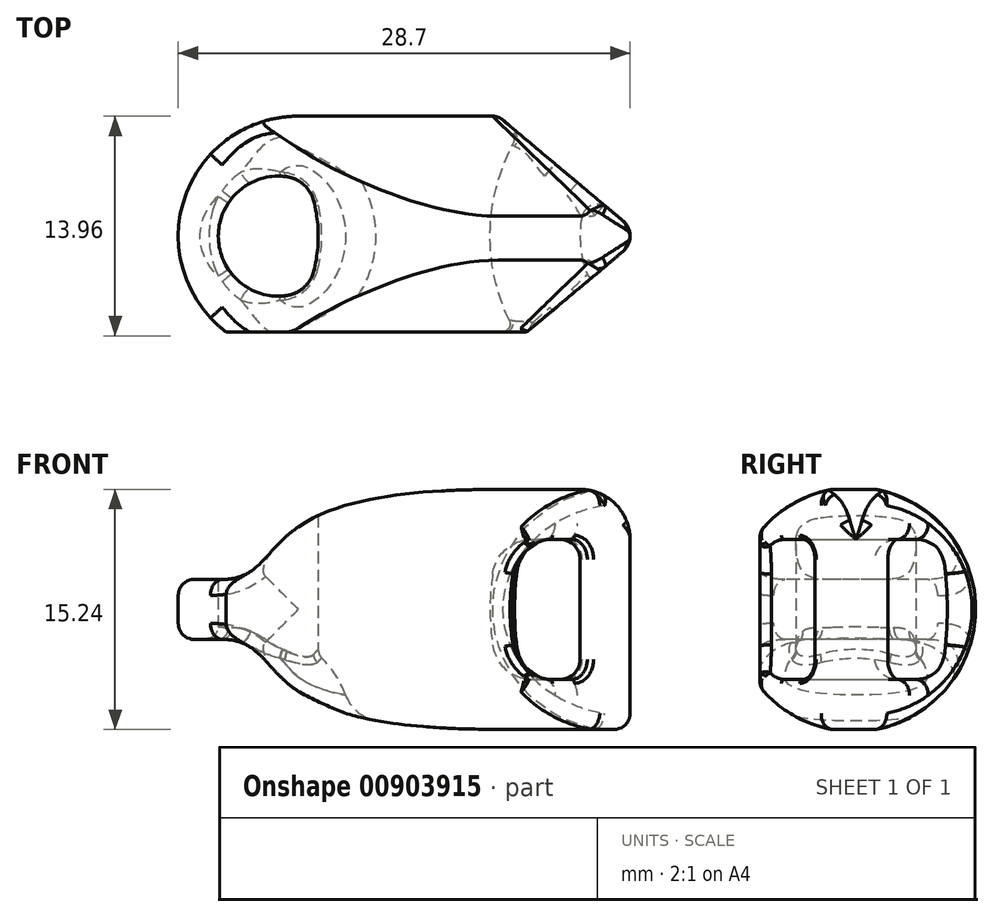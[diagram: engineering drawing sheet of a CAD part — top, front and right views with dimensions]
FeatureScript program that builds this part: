
annotation { "Feature Type Name" : "Feature", "Feature Type Description" : "" }
export const myFeature = defineFeature(function(context is Context, id is Id, definition is map)
    precondition{}
    {
        {
            var Q0;
            Q0=qCreatedBy(makeId("Top.planeOp"),FACE);
            var sketch = newSketch(context, id + "F0", { "sketchPlane" : qUnion([Q0])});
            skLineSegment(sketch, "E0", {"start": v(-6.35, 15.24) * mm, "end": v(6.35, 15.24) * mm});
            skLineSegment(sketch, "E1", {"start": v(-6.35, 0) * mm, "end": v(6.35, 0) * mm});
            skLineSegment(sketch, "E2", {"start": v(6.35, 0) * mm, "end": v(15.43, 7.62) * mm});
            skLineSegment(sketch, "E3", {"start": v(15.43, 7.62) * mm, "end": v(6.35, 15.24) * mm});
            skArc(sketch, "E4", {"start": v(-6.35, 15.24) * mm, "mid": v(-13.97, 7.62) * mm, "end": v(-6.35, 0) * mm});
            skSolve(sketch);
        }
        {
            var Q0;
            Q0 = qSketchRegion(id + "F0", true);
            extrude(context, id + "F1", {"entities" : qUnion([Q0]), "depth" : 15.24 * mm, "offsetDistance" : 25.4 * mm});
        }
        {
            var Q0;
            Q0=makeQuery(id+"F1.opExtrude","SWEPT_EDGE",EDGE,{"disambiguationData":[OSD([sQuery(id+"F0.wireOp",EDGE,"E2"),sQuery(id+"F0.wireOp",EDGE,"E3")])]});
            fillet(context, id + "F2", {"entities" : qUnion([Q0]), "radius" : 1.27 * mm, "tangentPropagation" : true, "allowEdgeOverflow" : false});
        }
        {
            var Q0;
            Q0=qCreatedBy(makeId("Front.planeOp"),FACE);
            cPlane(context, id + "F3", {"entities" : qUnion([Q0]), "cplaneType" : CPlaneType.OFFSET, "offset" : 7.62 * mm, "oppositeDirection" : true, "width" : 152.4 * mm, "height" : 152.4 * mm});
        }
        {
            var Q0;
            Q0=qCreatedBy(id+"F3.planeOp",FACE);
            var sketch = newSketch(context, id + "F4", { "sketchPlane" : qUnion([Q0])});
            skArc(sketch, "E5", {"start": v(6, 9.89) * mm, "mid": v(5.84, 7.62) * mm, "end": v(6, 5.35) * mm});
            skLineSegment(sketch, "E6", {"start": v(11.55, 4.45) * mm, "end": v(11.55, 10.8) * mm});
            skLineSegment(sketch, "E7.0.0", {"start": v(14.27, 15.24) * mm, "end": v(14.73, 15.24) * mm, "construction": true});
            skLineSegment(sketch, "E7.0.1", {"start": v(14.27, 0) * mm, "end": v(14.27, 15.24) * mm, "construction": true});
            skLineSegment(sketch, "E7.0.2", {"start": v(14.27, 0) * mm, "end": v(14.73, 0) * mm, "construction": true});
            skLineSegment(sketch, "E7.0.3", {"start": v(14.27, 0) * mm, "end": v(14.27, 15.24) * mm, "construction": true});
            skLineSegment(sketch, "E8", {"start": v(10.28, 12.06) * mm, "end": v(8.51, 12.06) * mm});
            skLineSegment(sketch, "E9", {"start": v(10.28, 3.17) * mm, "end": v(8.51, 3.17) * mm});
            skPoint(sketch, "E10.visualSharp", {"position": v(6.47, 12.06) * mm});
            skArc(sketch, "E10.filletArc", {"start": v(8.51, 12.06) * mm, "mid": v(6.85, 11.45) * mm, "end": v(6, 9.89) * mm});
            skPoint(sketch, "E11.visualSharp", {"position": v(6.47, 3.17) * mm});
            skArc(sketch, "E11.filletArc", {"start": v(6, 5.35) * mm, "mid": v(6.85, 3.8) * mm, "end": v(8.51, 3.17) * mm});
            skPoint(sketch, "E12.visualSharp", {"position": v(11.55, 3.18) * mm});
            skArc(sketch, "E12.filletArc", {"start": v(10.28, 3.17) * mm, "mid": v(11.18, 3.55) * mm, "end": v(11.55, 4.45) * mm});
            skPoint(sketch, "E13.visualSharp", {"position": v(11.55, 12.06) * mm});
            skArc(sketch, "E13.filletArc", {"start": v(11.55, 10.8) * mm, "mid": v(11.18, 11.7) * mm, "end": v(10.28, 12.06) * mm});
            skLineSegment(sketch, "E14", {"start": v(18.27, 11.8) * mm, "end": v(18.27, -2.1) * mm, "construction": true});
            skSolve(sketch);
        }
        {
            var Q0;
            Q0 = qSketchRegion(id + "F4", true);
            var Q1;
            Q1=sQuery(id+"F4.wireOp",EDGE,"E14");
            revolve(context, id + "F5", {"operationType" : NewBodyOperationType.REMOVE, "surfaceOperationType" : NewSurfaceOperationType.NEW, "entities" : qUnion([Q0]), "axis" : qUnion([Q1]), "revolveType" : RevolveType.FULL, "oppositeDirection" : true});
        }
        {
            var Q0;
            Q0=makeQuery(id+"F1.opExtrude","SWEPT_FACE",FACE,{"disambiguationData":[OSD([sQuery(id+"F0.wireOp",EDGE,"E1")])]});
            var sketch = newSketch(context, id + "F6", { "sketchPlane" : qUnion([Q0])});
            skLineSegment(sketch, "E15", {"start": v(-15.35, 7.62) * mm, "end": v(17.07, 7.62) * mm, "construction": true});
            skLineSegment(sketch, "E16.0", {"start": v(-15.35, 5.71) * mm, "end": v(17.07, 5.71) * mm, "construction": true});
            skLineSegment(sketch, "E17.0", {"start": v(-15.35, 9.53) * mm, "end": v(17.07, 9.53) * mm, "construction": true});
            skLineSegment(sketch, "E18.0", {"start": v(11.8, 11.94) * mm, "end": v(11.8, 11.94) * mm});
            skPoint(sketch, "E19.first.point", {"position": v(-13.97, 9.53) * mm});
            skLineSegment(sketch, "E20.0", {"start": v(-6.35, 15.24) * mm, "end": v(6.35, 15.24) * mm, "construction": true});
            skLineSegment(sketch, "E21.0", {"start": v(-6.35, 0) * mm, "end": v(-13.97, 0) * mm, "construction": true});
            skLineSegment(sketch, "E22", {"start": v(-13.97, 0) * mm, "end": v(-13.97, 14.89) * mm, "construction": true});
            skLineSegment(sketch, "E23.0", {"start": v(-6.35, 0) * mm, "end": v(2.29, 0) * mm, "construction": true});
            skLineSegment(sketch, "E24", {"start": v(-11.18, 9.53) * mm, "end": v(-16.26, 9.53) * mm});
            skLineSegment(sketch, "E25", {"start": v(-16.26, 9.53) * mm, "end": v(-15.86, 16.25) * mm});
            skLineSegment(sketch, "E26.MirrorCS", {"start": v(-15.35, 5.72) * mm, "end": v(17.07, 5.72) * mm, "construction": true});
            skLineSegment(sketch, "E27.MirrorCS", {"start": v(-16.26, 5.72) * mm, "end": v(-15.86, -1) * mm});
            skLineSegment(sketch, "E28.MirrorCS", {"start": v(-11.18, 5.71) * mm, "end": v(-16.26, 5.71) * mm});
            skFitSpline(sketch, "E29", {"points": [v(6.35, 15.24) * mm, v(-8.08, 11.26) * mm, v(-11.18, 9.53) * mm], "startDerivative": vector(-47.28, 0) * mm, "endDerivative": vector(-14.56, 0) * mm});
            skLineSegment(sketch, "E30", {"start": v(-15.86, 16.25) * mm, "end": v(6.35, 15.24) * mm});
            skLineSegment(sketch, "E31.MirrorCS", {"start": v(-15.86, -1) * mm, "end": v(6.35, 0) * mm});
            skFitSpline(sketch, "E32.MirrorCS", {"points": [v(6.35, 0) * mm, v(-8.08, 3.98) * mm, v(-11.18, 5.71) * mm], "startDerivative": vector(-47.28, 0) * mm, "endDerivative": vector(-14.56, 0) * mm});
            skSolve(sketch);
        }
        {
            var Q0;
            Q0 = qSketchRegion(id + "F6", true);
            extrude(context, id + "F7", {"entities" : qUnion([Q0]), "operationType" : NewBodyOperationType.REMOVE, "oppositeDirection" : true, "depth" : 25.4 * mm, "offsetDistance" : 25.4 * mm});
        }
        {
            var Q0;
            Q0=qCreatedBy(makeId("Right.planeOp"),FACE);
            var sketch = newSketch(context, id + "F8", { "sketchPlane" : qUnion([Q0])});
            skCircle(sketch, "E33", {"center": v(7.5, 7.62) * mm, "radius": 16.21 * mm});
            skLineSegment(sketch, "E34.0", {"start": v(15.24, 12.86) * mm, "end": v(15.24, 12.86) * mm});
            skLineSegment(sketch, "E34.1", {"start": v(15.24, 15.24) * mm, "end": v(0, 15.24) * mm, "construction": true});
            skLineSegment(sketch, "E34.2", {"start": v(0, 12.86) * mm, "end": v(0, 2.38) * mm, "construction": true});
            skLineSegment(sketch, "E34.3", {"start": v(15.24, 0) * mm, "end": v(0, 0) * mm, "construction": true});
            skArc(sketch, "E35", {"start": v(1.52, 2.68) * mm, "mid": v(15.24, 7.62) * mm, "end": v(1.52, 12.56) * mm});
            skLineSegment(sketch, "E36", {"start": v(1.52, 12.56) * mm, "end": v(1.52, 2.68) * mm});
            skSolve(sketch);
        }
        {
            var Q0;
            Q0 = qSketchRegion(id + "F8", true);
            extrude(context, id + "F9", {"entities" : qUnion([Q0]), "operationType" : NewBodyOperationType.REMOVE, "endBound" : BoundingType.SYMMETRIC, "oppositeDirection" : true, "depth" : 127 * mm, "offsetDistance" : 25.4 * mm});
        }
        {
            var Q0;
            Q0=makeQuery(id+"F7.boolean.opBoolean","COPY",FACE,{"derivedFrom":makeQuery(id+"F7.opExtrude","SWEPT_FACE",FACE,{"disambiguationData":[OSD([sQuery(id+"F6.wireOp",EDGE,"E28.MirrorCS")])]})});
            var sketch = newSketch(context, id + "F10", { "sketchPlane" : qUnion([Q0])});
            skLineSegment(sketch, "E37.0", {"start": v(-11.18, -1.72) * mm, "end": v(-11.18, -1.72) * mm});
            skArc(sketch, "E38", {"start": v(-5.37, -9.87) * mm, "mid": v(-5.08, -7.62) * mm, "end": v(-5.37, -5.37) * mm});
            skLineSegment(sketch, "E39", {"start": v(-7.37, -0.39) * mm, "end": v(-7.37, -15.77) * mm, "construction": true});
            skArc(sketch, "E40", {"start": v(-7.07, -3.85) * mm, "mid": v(-11.43, -7.62) * mm, "end": v(-7.07, -11.39) * mm});
            skArc(sketch, "E41", {"start": v(-5.37, -5.37) * mm, "mid": v(-5.99, -4.36) * mm, "end": v(-7.07, -3.85) * mm});
            skArc(sketch, "E42", {"start": v(-7.07, -11.39) * mm, "mid": v(-5.99, -10.88) * mm, "end": v(-5.37, -9.87) * mm});
            skSolve(sketch);
        }
        {
            var Q0;
            Q0 = qSketchRegion(id + "F10", true);
            extrude(context, id + "F11", {"entities" : qUnion([Q0]), "operationType" : NewBodyOperationType.REMOVE, "endBound" : BoundingType.SYMMETRIC, "oppositeDirection" : true, "depth" : 25.4 * mm, "offsetDistance" : 25.4 * mm});
        }
        {
            var Q0;
            Q0=qCreatedBy(makeId("Front.planeOp"),FACE);
            cPlane(context, id + "F12", {"entities" : qUnion([Q0]), "cplaneType" : CPlaneType.OFFSET, "offset" : 2.54 * mm, "oppositeDirection" : true, "width" : 152.4 * mm, "height" : 152.4 * mm});
        }
        {
            var Q0;
            Q0=qCreatedBy(id+"F12.planeOp",FACE);
            var sketch = newSketch(context, id + "F13", { "sketchPlane" : qUnion([Q0])});
            skCircle(sketch, "E43", {"center": v(0, 4.3) * mm, "radius": 43.05 * mm});
            skSolve(sketch);
        }
        {
            var Q0;
            Q0=qCreatedBy(makeId("Top.planeOp"),FACE);
            var sketch = newSketch(context, id + "F14", { "sketchPlane" : qUnion([Q0])});
            skArc(sketch, "E44", {"start": v(-9.3, 1.27) * mm, "mid": v(-2.96, 7.62) * mm, "end": v(-9.3, 13.97) * mm});
            skLineSegment(sketch, "E45", {"start": v(-9.3, 17.15) * mm, "end": v(-9.3, 13.97) * mm, "construction": true});
            skLineSegment(sketch, "E46", {"start": v(-9.3, 13.97) * mm, "end": v(-9.3, 1.27) * mm});
            skSolve(sketch);
        }
        {
            var Q0;
            Q0=makeQuery(id+"F14.imprint","IMPRINT",FACE,{"disambiguationData":[TD([[makeQuery(id+"F14.imprint","IMPRINT",EDGE,{"derivedFrom":sQuery(id+"F14.wireOp",EDGE,"E44")}),1.0]])]});
            var Q1;
            Q1=sQuery(id+"F14.wireOp",EDGE,"E45");
            revolve(context, id + "F15", {"operationType" : NewBodyOperationType.REMOVE, "surfaceOperationType" : NewSurfaceOperationType.NEW, "entities" : qUnion([Q0]), "axis" : qUnion([Q1]), "revolveType" : RevolveType.FULL, "oppositeDirection" : true});
        }
        {
            var Q0;
            Q0=qCreatedBy(makeId("Top.planeOp"),FACE);
            cPlane(context, id + "F16", {"entities" : qUnion([Q0]), "cplaneType" : CPlaneType.OFFSET, "offset" : 7.62 * mm, "width" : 152.4 * mm, "height" : 152.4 * mm});
        }
        {
            var Q0;
            Q0=makeQuery(id+"FS2piOo9BQHkGEu_1.1.F15.boolean.opBoolean","INTERSECT",EDGE,{"disambiguationData":[OD(1.0)],"derivedFrom":[makeQuery(id+"F7.boolean.opBoolean","COPY",FACE,{"derivedFrom":makeQuery(id+"F7.opExtrude","SWEPT_FACE",FACE,{"disambiguationData":[OSD([sQuery(id+"F6.wireOp",EDGE,"E29")])]})}),makeQuery(id+"FS2piOo9BQHkGEu_1.1.F15.opRevolve","SWEPT_FACE",FACE,{"disambiguationData":[OSD([sQuery(id+"F14.wireOp",EDGE,"E44")])]})]});
            var Q1;
            Q1=makeQuery(id+"F15.boolean.opBoolean","INTERSECT",EDGE,{"disambiguationData":[OD(1.0)],"derivedFrom":[makeQuery(id+"F7.boolean.opBoolean","COPY",FACE,{"derivedFrom":makeQuery(id+"F7.opExtrude","SWEPT_FACE",FACE,{"disambiguationData":[OSD([sQuery(id+"F6.wireOp",EDGE,"E32.MirrorCS")])]})}),makeQuery(id+"F15.opRevolve","SWEPT_FACE",FACE,{"disambiguationData":[OSD([sQuery(id+"F14.wireOp",EDGE,"E44")])]})]});
            fillet(context, id + "F17", {"entities" : qUnion([Q0, Q1]), "radius" : 2.54 * mm, "allowEdgeOverflow" : false});
        }
        {
            var Q0;
            Q0=makeQuery(id+"F7.boolean.opBoolean","INTERSECT",EDGE,{"derivedFrom":[makeQuery(id+"F1.opExtrude","SWEPT_FACE",FACE,{"disambiguationData":[OSD([sQuery(id+"F0.wireOp",EDGE,"E4")])]}),makeQuery(id+"F7.opExtrude","SWEPT_FACE",FACE,{"disambiguationData":[OSD([sQuery(id+"F6.wireOp",EDGE,"E24")])]})]});
            var Q1;
            Q1=makeQuery(id+"F7.boolean.opBoolean","INTERSECT",EDGE,{"derivedFrom":[makeQuery(id+"F1.opExtrude","SWEPT_FACE",FACE,{"disambiguationData":[OSD([sQuery(id+"F0.wireOp",EDGE,"E4")])]}),makeQuery(id+"F7.opExtrude","SWEPT_FACE",FACE,{"disambiguationData":[OSD([sQuery(id+"F6.wireOp",EDGE,"E28.MirrorCS")])]})]});
            var Q2;
            Q2=makeQuery(id+"F9.boolean.opBoolean","INTERSECT",EDGE,{"disambiguationData":[OD(1.0)],"derivedFrom":[makeQuery(id+"F1.opExtrude","SWEPT_FACE",FACE,{"disambiguationData":[OSD([sQuery(id+"F0.wireOp",EDGE,"E3")])]}),makeQuery(id+"F9.opExtrude","SWEPT_FACE",FACE,{"disambiguationData":[OSD([sQuery(id+"F8.wireOp",EDGE,"E35")])]})]});
            var Q3;
            {var subQ0=sQuery(id+"F0.wireOp",EDGE,"E3");var subQ1=sQuery(id+"F0.wireOp",EDGE,"E2");Q3=makeQuery(id+"F2.opFillet","BLEND_EDGE",EDGE,{"blendedFrom":[makeQuery(id+"F1.opExtrude","SWEPT_EDGE",EDGE,{"disambiguationData":[OSD([subQ1,subQ0])]}),makeQuery(id+"F1.opExtrude","CAP_FACE",FACE,{"disambiguationData":[OSD([sQuery(id+"F0.wireOp",EDGE,"E0"),sQuery(id+"F0.wireOp",EDGE,"E1"),subQ1,subQ0,sQuery(id+"F0.wireOp",EDGE,"E4")])],"isStart":false})],"blendedInto":[makeQuery(id+"F1.opExtrude","CAP_FACE",FACE,{"disambiguationData":[OSD([sQuery(id+"F0.wireOp",EDGE,"E0"),sQuery(id+"F0.wireOp",EDGE,"E1"),subQ1,subQ0,sQuery(id+"F0.wireOp",EDGE,"E4")])],"isStart":false})]});}
            var Q4;
            Q4=makeQuery(id+"F9.boolean.opBoolean","INTERSECT",EDGE,{"disambiguationData":[OD(0.0)],"derivedFrom":[makeQuery(id+"F1.opExtrude","SWEPT_FACE",FACE,{"disambiguationData":[OSD([sQuery(id+"F0.wireOp",EDGE,"E3")])]}),makeQuery(id+"F9.opExtrude","SWEPT_FACE",FACE,{"disambiguationData":[OSD([sQuery(id+"F8.wireOp",EDGE,"E35")])]})]});
            var Q5;
            {var subQ0=sQuery(id+"F0.wireOp",EDGE,"E3");var subQ1=sQuery(id+"F0.wireOp",EDGE,"E2");Q5=makeQuery(id+"F2.opFillet","BLEND_EDGE",EDGE,{"blendedFrom":[makeQuery(id+"F1.opExtrude","SWEPT_EDGE",EDGE,{"disambiguationData":[OSD([subQ1,subQ0])]}),makeQuery(id+"F1.opExtrude","CAP_FACE",FACE,{"disambiguationData":[OSD([sQuery(id+"F0.wireOp",EDGE,"E0"),sQuery(id+"F0.wireOp",EDGE,"E1"),subQ1,subQ0,sQuery(id+"F0.wireOp",EDGE,"E4")])],"isStart":true})],"blendedInto":[makeQuery(id+"F1.opExtrude","CAP_FACE",FACE,{"disambiguationData":[OSD([sQuery(id+"F0.wireOp",EDGE,"E0"),sQuery(id+"F0.wireOp",EDGE,"E1"),subQ1,subQ0,sQuery(id+"F0.wireOp",EDGE,"E4")])],"isStart":true})]});}
            var Q6;
            Q6=makeQuery(id+"F9.boolean.opBoolean","INTERSECT",EDGE,{"disambiguationData":[OD(0.0)],"derivedFrom":[makeQuery(id+"F1.opExtrude","SWEPT_FACE",FACE,{"disambiguationData":[OSD([sQuery(id+"F0.wireOp",EDGE,"E2")])]}),makeQuery(id+"F9.opExtrude","SWEPT_FACE",FACE,{"disambiguationData":[OSD([sQuery(id+"F8.wireOp",EDGE,"E35")])]})]});
            var Q7;
            Q7=makeQuery(id+"F9.boolean.opBoolean","INTERSECT",EDGE,{"disambiguationData":[OD(1.0)],"derivedFrom":[makeQuery(id+"F1.opExtrude","SWEPT_FACE",FACE,{"disambiguationData":[OSD([sQuery(id+"F0.wireOp",EDGE,"E2")])]}),makeQuery(id+"F9.opExtrude","SWEPT_FACE",FACE,{"disambiguationData":[OSD([sQuery(id+"F8.wireOp",EDGE,"E35")])]})]});
            var Q8;
            {var subQ0=sQuery(id+"F8.wireOp",EDGE,"E36");var subQ1=sQuery(id+"F8.wireOp",EDGE,"E35");Q8=makeQuery(id+"F9.boolean.opBoolean","COPY",EDGE,{"derivedFrom":makeQuery(id+"F9.opExtrude","SWEPT_EDGE",EDGE,{"disambiguationData":[OSD([subQ1,subQ0]),TDD([makeQuery(id+"F8.imprint","INTERSECT",VERTEX,{"disambiguationData":[OD(1.0)],"derivedFrom":[subQ1,subQ0]})])]})});}
            var Q9;
            {var subQ0=sQuery(id+"F8.wireOp",EDGE,"E36");var subQ1=sQuery(id+"F8.wireOp",EDGE,"E35");Q9=makeQuery(id+"F9.boolean.opBoolean","COPY",EDGE,{"derivedFrom":makeQuery(id+"F9.opExtrude","SWEPT_EDGE",EDGE,{"disambiguationData":[OSD([subQ1,subQ0]),TDD([makeQuery(id+"F8.imprint","INTERSECT",VERTEX,{"disambiguationData":[OD(0.0)],"derivedFrom":[subQ1,subQ0]})])]})});}
            var Q10;
            Q10=makeQuery(id+"F9.boolean.opBoolean","INTERSECT",EDGE,{"disambiguationData":[OD(0.0)],"derivedFrom":[makeQuery(id+"F1.opExtrude","SWEPT_FACE",FACE,{"disambiguationData":[OSD([sQuery(id+"F0.wireOp",EDGE,"E0")])]}),makeQuery(id+"F9.opExtrude","SWEPT_FACE",FACE,{"disambiguationData":[OSD([sQuery(id+"F8.wireOp",EDGE,"E35")])]})]});
            var Q11;
            Q11=makeQuery(id+"F9.boolean.opBoolean","INTERSECT",EDGE,{"disambiguationData":[OD(1.0)],"derivedFrom":[makeQuery(id+"F1.opExtrude","SWEPT_FACE",FACE,{"disambiguationData":[OSD([sQuery(id+"F0.wireOp",EDGE,"E0")])]}),makeQuery(id+"F9.opExtrude","SWEPT_FACE",FACE,{"disambiguationData":[OSD([sQuery(id+"F8.wireOp",EDGE,"E35")])]})]});
            var Q12;
            Q12=makeQuery(id+"F1.opExtrude","SWEPT_EDGE",EDGE,{"disambiguationData":[OSD([sQuery(id+"F0.wireOp",EDGE,"E0"),sQuery(id+"F0.wireOp",EDGE,"E3")])]});
            fillet(context, id + "F18", {"entities" : qUnion([Q0, Q1, Q2, Q3, Q4, Q5, Q6, Q7, Q8, Q9, Q10, Q11, Q12]), "radius" : 1.02 * mm, "tangentPropagation" : true, "allowEdgeOverflow" : false});
        }
        {
            var Q0;
            Q0=makeQuery(id+"F5.boolean.opBoolean","INTERSECT",EDGE,{"derivedFrom":[makeQuery(id+"F1.opExtrude","SWEPT_FACE",FACE,{"disambiguationData":[OSD([sQuery(id+"F0.wireOp",EDGE,"E3")])]}),makeQuery(id+"F5.opRevolve","SWEPT_FACE",FACE,{"disambiguationData":[OSD([sQuery(id+"F4.wireOp",EDGE,"E6")])]})]});
            fillet(context, id + "F19", {"entities" : qUnion([Q0]), "radius" : 1.02 * mm, "tangentPropagation" : true, "allowEdgeOverflow" : false});
        }
        {
            var Q0;
            Q0=makeQuery(id+"F5.boolean.opBoolean","INTERSECT",EDGE,{"derivedFrom":[makeQuery(id+"F1.opExtrude","SWEPT_FACE",FACE,{"disambiguationData":[OSD([sQuery(id+"F0.wireOp",EDGE,"E2")])]}),makeQuery(id+"F5.opRevolve","SWEPT_FACE",FACE,{"disambiguationData":[OSD([sQuery(id+"F4.wireOp",EDGE,"E6")])]})]});
            fillet(context, id + "F20", {"entities" : qUnion([Q0]), "radius" : 0.25 * mm, "tangentPropagation" : true, "allowEdgeOverflow" : false});
        }
        {
            var Q0;
            Q0=makeQuery(id+"F13.imprint","IMPRINT",FACE,{"disambiguationData":[TD([[makeQuery(id+"F13.imprint","IMPRINT",EDGE,{"derivedFrom":sQuery(id+"F13.wireOp",EDGE,"E43")}),1.0]])]});
            var Q1;
            Q1=makeQuery(id+"F13.imprint","IMPRINT",FACE,{"disambiguationData":[TD([[makeQuery(id+"F13.imprint","IMPRINT",EDGE,{"derivedFrom":sQuery(id+"F13.wireOp",EDGE,"E43")}),1.0]])]});
            var sketch = newSketch(context, id + "F21", { "sketchPlane" : qUnion([Q0, Q1])});
            skLineSegment(sketch, "E47.0", {"start": v(12.34, 15.24) * mm, "end": v(6.35, 15.24) * mm, "construction": true});
            skLineSegment(sketch, "E48.0.0", {"start": v(14.27, 1.02) * mm, "end": v(14.27, 14.22) * mm, "construction": true});
            skLineSegment(sketch, "E48.0.1", {"start": v(14.27, 14.22) * mm, "end": v(14.73, 14.22) * mm, "construction": true});
            skLineSegment(sketch, "E48.0.2", {"start": v(14.27, 1.02) * mm, "end": v(14.27, 14.22) * mm, "construction": true});
            skLineSegment(sketch, "E48.0.3", {"start": v(14.27, 1.02) * mm, "end": v(14.73, 1.02) * mm, "construction": true});
            skLineSegment(sketch, "E49", {"start": v(14.73, 14.22) * mm, "end": v(14.73, 6.34) * mm, "construction": true});
            skArc(sketch, "E50", {"start": v(14.73, 12.06) * mm, "mid": v(13.8, 14.31) * mm, "end": v(11.55, 15.24) * mm});
            skLineSegment(sketch, "E51", {"start": v(14.73, 12.06) * mm, "end": v(16.27, 13.58) * mm});
            skLineSegment(sketch, "E52", {"start": v(16.27, 13.58) * mm, "end": v(14.73, 15.97) * mm});
            skLineSegment(sketch, "E53", {"start": v(14.73, 15.97) * mm, "end": v(11.55, 15.24) * mm});
            skSolve(sketch);
        }
        {
            var Q0;
            Q0 = qSketchRegion(id + "F21", true);
            extrude(context, id + "F22", {"entities" : qUnion([Q0]), "operationType" : NewBodyOperationType.REMOVE, "endBound" : BoundingType.THROUGH_ALL, "oppositeDirection" : true, "depth" : 25.4 * mm, "offsetDistance" : 25.4 * mm});
        }
        {
            var Q0;
            Q0=makeQuery(id+"F22.boolean.opBoolean","INTERSECT",EDGE,{"disambiguationData":[OD(1.0)],"derivedFrom":[makeQuery(id+"F2.opFillet","BLEND_FACE",FACE,{"disambiguationData":[OSD([sQuery(id+"F0.wireOp",EDGE,"E2"),sQuery(id+"F0.wireOp",EDGE,"E3")])]}),makeQuery(id+"F22.opExtrude","SWEPT_FACE",FACE,{"disambiguationData":[OSD([sQuery(id+"F21.wireOp",EDGE,"E50")])]})]});
            var Q1;
            Q1=makeQuery(id+"F22.boolean.opBoolean","INTERSECT",EDGE,{"disambiguationData":[OD(0.0)],"derivedFrom":[makeQuery(id+"F2.opFillet","BLEND_FACE",FACE,{"disambiguationData":[OSD([sQuery(id+"F0.wireOp",EDGE,"E2"),sQuery(id+"F0.wireOp",EDGE,"E3")])]}),makeQuery(id+"F22.opExtrude","SWEPT_FACE",FACE,{"disambiguationData":[OSD([sQuery(id+"F21.wireOp",EDGE,"E50")])]})]});
            var Q2;
            Q2=makeQuery(id+"FD36omhEUi3x7Mn_1.1.F22.boolean.opBoolean","INTERSECT",EDGE,{"disambiguationData":[OD(1.0)],"derivedFrom":[makeQuery(id+"F2.opFillet","BLEND_FACE",FACE,{"disambiguationData":[OSD([sQuery(id+"F0.wireOp",EDGE,"E2"),sQuery(id+"F0.wireOp",EDGE,"E3")])]}),makeQuery(id+"FD36omhEUi3x7Mn_1.1.F22.opExtrude","SWEPT_FACE",FACE,{"disambiguationData":[OSD([sQuery(id+"F21.wireOp",EDGE,"E50")])]})]});
            var Q3;
            Q3=makeQuery(id+"FD36omhEUi3x7Mn_1.1.F22.boolean.opBoolean","INTERSECT",EDGE,{"disambiguationData":[OD(0.0)],"derivedFrom":[makeQuery(id+"F2.opFillet","BLEND_FACE",FACE,{"disambiguationData":[OSD([sQuery(id+"F0.wireOp",EDGE,"E2"),sQuery(id+"F0.wireOp",EDGE,"E3")])]}),makeQuery(id+"FD36omhEUi3x7Mn_1.1.F22.opExtrude","SWEPT_FACE",FACE,{"disambiguationData":[OSD([sQuery(id+"F21.wireOp",EDGE,"E50")])]})]});
            fillet(context, id + "F23", {"entities" : qUnion([Q0, Q1, Q2, Q3]), "radius" : 0.76 * mm, "tangentPropagation" : true, "allowEdgeOverflow" : false});
        }
        {
            var Q0;
            Q0=makeQuery(id+"F9.boolean.opBoolean","INTERSECT",EDGE,{"derivedFrom":[makeQuery(id+"F5.boolean.opBoolean","COPY",FACE,{"derivedFrom":makeQuery(id+"F5.opRevolve","SWEPT_FACE",FACE,{"disambiguationData":[OSD([sQuery(id+"F4.wireOp",EDGE,"E5")])]})}),makeQuery(id+"F9.opExtrude","SWEPT_FACE",FACE,{"disambiguationData":[OSD([sQuery(id+"F8.wireOp",EDGE,"E36")])]})]});
            fillet(context, id + "F24", {"entities" : qUnion([Q0]), "radius" : 0.5 * mm, "tangentPropagation" : true, "allowEdgeOverflow" : false});
        }
        {
            var Q0;
            Q0=makeQuery(id+"FS2piOo9BQHkGEu_1.1.F15.boolean.opBoolean","INTERSECT",EDGE,{"derivedFrom":[makeQuery(id+"F11.boolean.opBoolean","COPY",FACE,{"derivedFrom":makeQuery(id+"F11.opExtrude","SWEPT_FACE",FACE,{"disambiguationData":[OSD([sQuery(id+"F10.wireOp",EDGE,"E38")])]})}),makeQuery(id+"FS2piOo9BQHkGEu_1.1.F15.opRevolve","SWEPT_FACE",FACE,{"disambiguationData":[OSD([sQuery(id+"F14.wireOp",EDGE,"E44")])]})]});
            var Q1;
            Q1=makeQuery(id+"F15.boolean.opBoolean","INTERSECT",EDGE,{"derivedFrom":[makeQuery(id+"F11.boolean.opBoolean","COPY",FACE,{"derivedFrom":makeQuery(id+"F11.opExtrude","SWEPT_FACE",FACE,{"disambiguationData":[OSD([sQuery(id+"F10.wireOp",EDGE,"E38")])]})}),makeQuery(id+"F15.opRevolve","SWEPT_FACE",FACE,{"disambiguationData":[OSD([sQuery(id+"F14.wireOp",EDGE,"E44")])]})]});
            fillet(context, id + "F25", {"entities" : qUnion([Q0, Q1]), "radius" : 0.76 * mm, "tangentPropagation" : true, "allowEdgeOverflow" : false});
        }
    });
